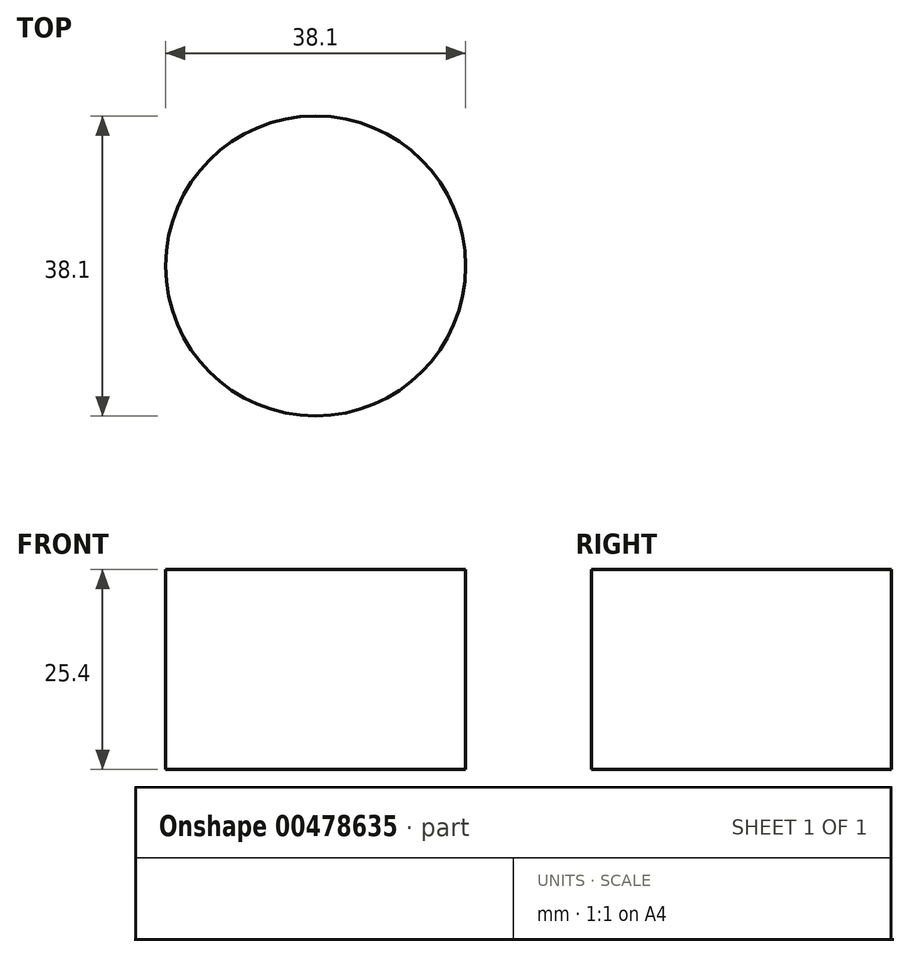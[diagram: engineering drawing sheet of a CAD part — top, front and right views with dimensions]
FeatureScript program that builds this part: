
annotation { "Feature Type Name" : "Feature", "Feature Type Description" : "" }
export const myFeature = defineFeature(function(context is Context, id is Id, definition is map)
    precondition{}
    {
        {
            var Q0;
            Q0=qCreatedBy(makeId("Top.planeOp"),FACE);
            var sketch = newSketch(context, id + "F0", { "sketchPlane" : qUnion([Q0])});
            skCircle(sketch, "E0", {"center": v(1.42, 0) * mm, "radius": 19.05 * mm});
            skSolve(sketch);
        }
        {
            var Q0;
            Q0=makeQuery(id+"F0.imprint","IMPRINT",FACE,{"disambiguationData":[TD([[makeQuery(id+"F0.imprint","IMPRINT",EDGE,{"derivedFrom":sQuery(id+"F0.wireOp",EDGE,"E0")}),1.0]])]});
            extrude(context, id + "F1", {"entities" : qUnion([Q0]), "depth" : 25.4 * mm, "offsetDistance" : 25.4 * mm});
        }
    });
